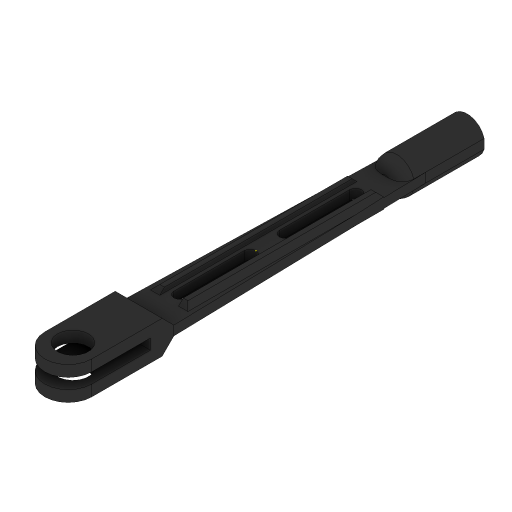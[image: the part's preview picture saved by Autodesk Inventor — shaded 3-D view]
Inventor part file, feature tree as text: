
AUTODESK INVENTOR PART (.ipt)
format: ipt  version: 2023 (Build 270158000, 158)  size: 688,128 bytes
history: native  units: mm
features: extrude x14, sketch x14, chamfer x5, fillet x3, other x1
ambient origin geometry x8: Origin, YZ Plane, XZ Plane, XY Plane, X Axis, Y Axis, Z Axis, Center Point
bodies: Body1 (feature_tree)
feature tree (37):
  other  "Bryła1"
  extrude  "Wyciągnięcie proste1"  Depth=20.0mm
  extrude  "Wyciągnięcie proste2"  Depth=180.0mm
  extrude  "Wyciągnięcie proste3"  Depth=4.0mm TaperAngle=0.0deg
  extrude  "Wyciągnięcie proste4"  Depth=4.0mm
  extrude  "Wyciągnięcie proste5"  Depth=10.0mm
  extrude  "Wyciągnięcie proste6"  Depth=4.0mm TaperAngle=0.0deg
  extrude  "Wyciągnięcie proste7"  Depth=45.0mm
  fillet  "Zaokrąglenie1"  Radius=5.0mm
  chamfer  "Faza1"  Distance=45.0mm
  chamfer  "Faza2"  Distance=5.0mm
  extrude  "Wyciągnięcie proste9"  Depth=35.0mm
  extrude  "Wyciągnięcie proste10"  Depth=4.5mm
  sketch  "Szkic12"
  extrude  "Wyciągnięcie proste11"  Depth=4.75mm
  fillet  "Zaokrąglenie2"  Radius=29.0mm
  extrude  "Wyciągnięcie proste12"  Depth=13.2mm
  fillet  "Zaokrąglenie3"  Radius=29.0mm
  chamfer  "Faza3"  Distance=12.0mm
  chamfer  "Faza4"  Distance=15.0mm
  sketch  "Szkic15"
  extrude  "Wyciągnięcie proste14"  Depth=2.0mm
  extrude  "Wyciągnięcie proste15"  Depth=10.0mm
  extrude  "Wyciągnięcie proste16"  Depth=25.0mm TaperAngle=0.0deg
  chamfer  "Faza5"  Distance=10.0mm
  sketch  "Szkic1"
  sketch  "Szkic2"
  sketch  "Szkic4"
  sketch  "Szkic5"
  sketch  "Szkic6"
  sketch  "Szkic7"
  sketch  "Szkic8"
  sketch  "Szkic10"
  sketch  "Szkic11"
  sketch  "Szkic13"
  sketch  "Szkic14"
  sketch  "Szkic16"
